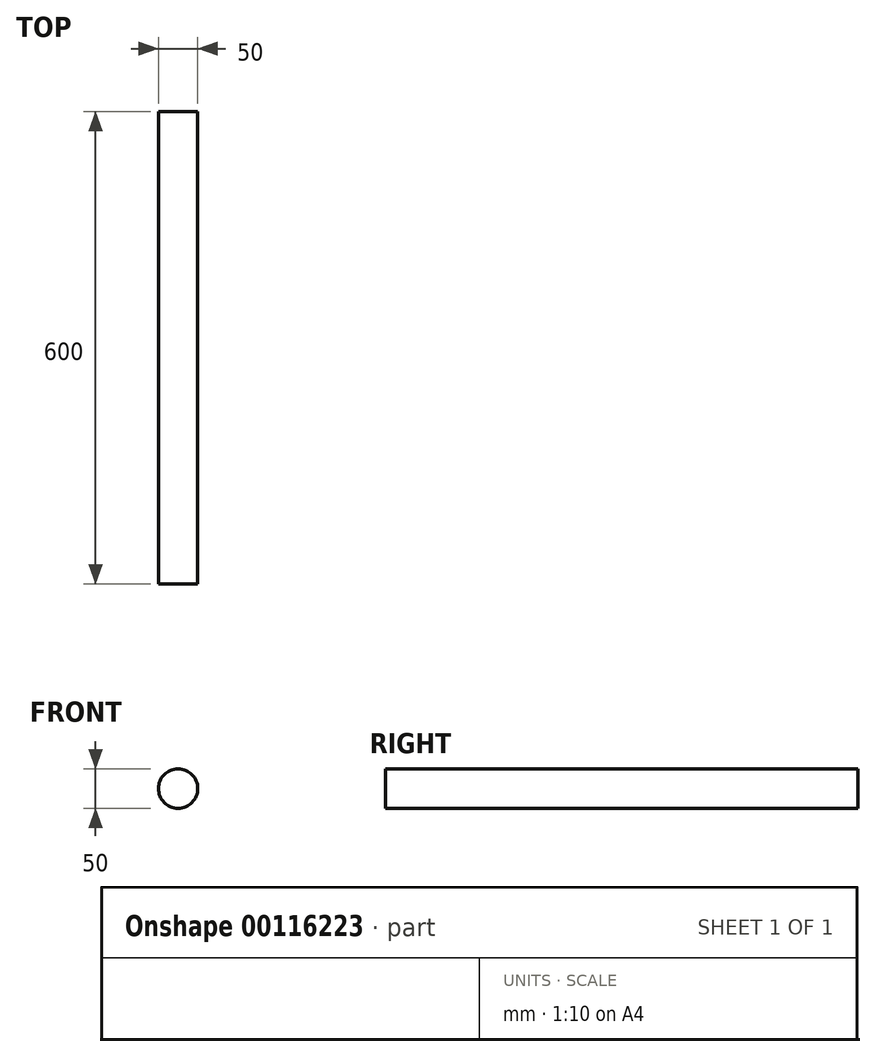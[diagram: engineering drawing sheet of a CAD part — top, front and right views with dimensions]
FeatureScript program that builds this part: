
annotation { "Feature Type Name" : "Feature", "Feature Type Description" : "" }
export const myFeature = defineFeature(function(context is Context, id is Id, definition is map)
    precondition{}
    {
        {
            var Q0;
            Q0=qCreatedBy(makeId("Front.planeOp"),FACE);
            var sketch = newSketch(context, id + "F0", { "sketchPlane" : qUnion([Q0])});
            skCircle(sketch, "E0", {"center": v(0, 0) * mm, "radius": 25 * mm});
            skSolve(sketch);
        }
        {
            var Q0;
            Q0=makeQuery(id+"F0.imprint","IMPRINT",FACE,{"disambiguationData":[TD([[makeQuery(id+"F0.imprint","IMPRINT",EDGE,{"derivedFrom":sQuery(id+"F0.wireOp",EDGE,"E0")}),1.0]])]});
            extrude(context, id + "F1", {"entities" : qUnion([Q0]), "depth" : 600 * mm});
        }
    });
